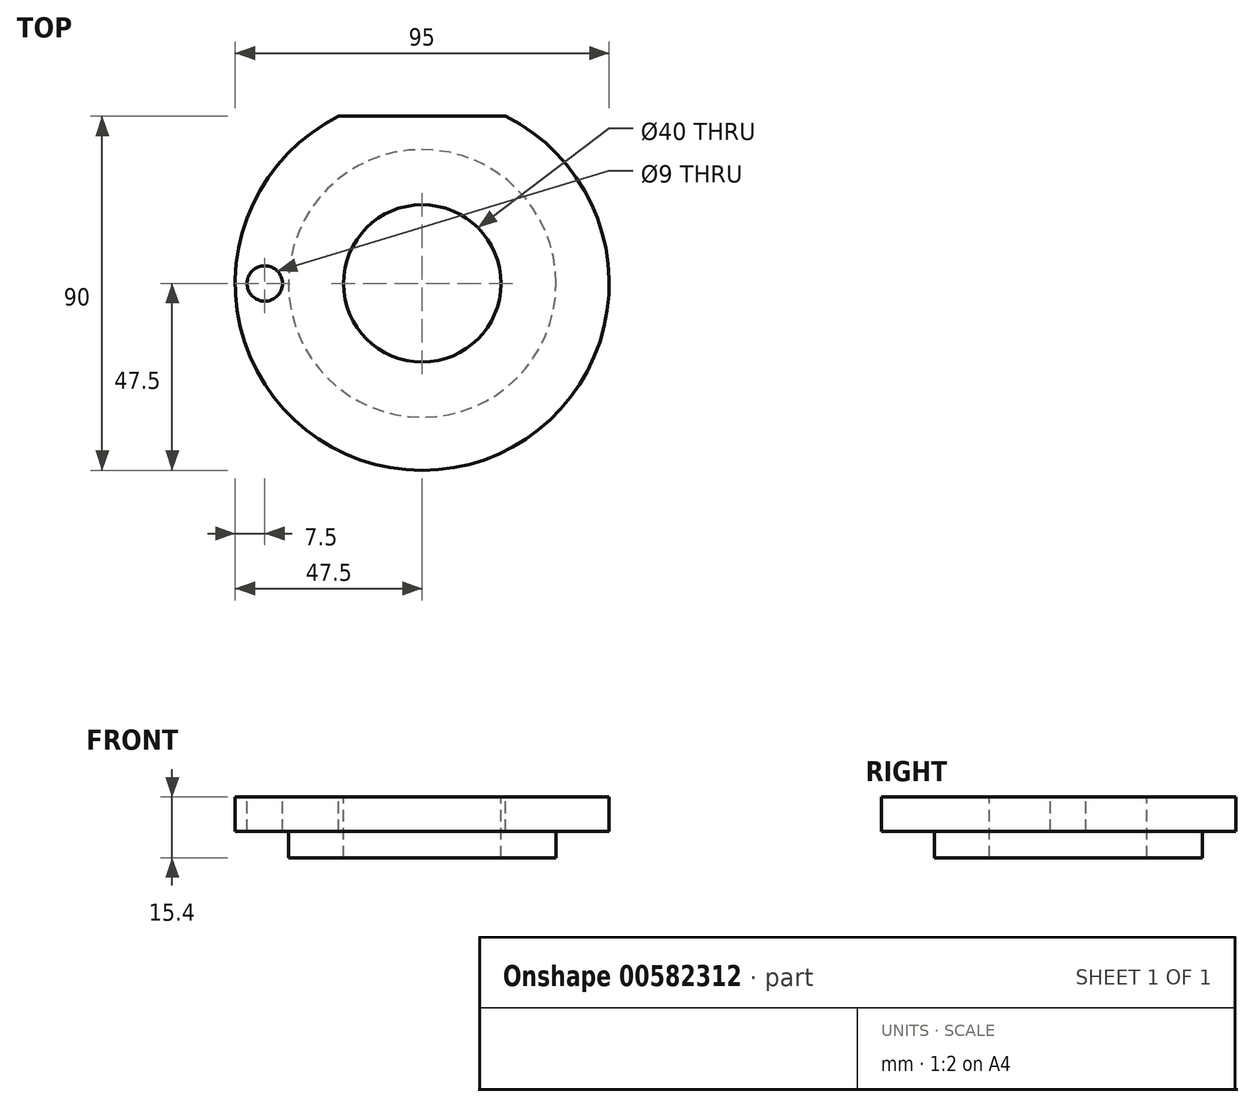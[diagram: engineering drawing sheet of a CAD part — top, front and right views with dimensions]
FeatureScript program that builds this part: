
annotation { "Feature Type Name" : "Feature", "Feature Type Description" : "" }
export const myFeature = defineFeature(function(context is Context, id is Id, definition is map)
    precondition{}
    {
        {
            var Q0;
            Q0=qCreatedBy(makeId("Top.planeOp"),FACE);
            var sketch = newSketch(context, id + "F0", { "sketchPlane" : qUnion([Q0])});
            skCircle(sketch, "E0", {"center": v(0, 0) * mm, "radius": 47.5 * mm});
            skSolve(sketch);
        }
        {
            var Q0;
            Q0=makeQuery(id+"F0.imprint","IMPRINT",FACE,{"disambiguationData":[TD([[makeQuery(id+"F0.imprint","IMPRINT",EDGE,{"derivedFrom":sQuery(id+"F0.wireOp",EDGE,"E0")}),1.0]])]});
            extrude(context, id + "F1", {"entities" : qUnion([Q0]), "oppositeDirection" : true, "depth" : 8.7 * mm, "offsetDistance" : 25 * mm});
        }
        {
            var Q0;
            Q0=makeQuery(id+"F1.opExtrude","CAP_FACE",FACE,{"disambiguationData":[OSD([sQuery(id+"F0.wireOp",EDGE,"E0")])],"isStart":true});
            var sketch = newSketch(context, id + "F2", { "sketchPlane" : qUnion([Q0])});
            skCircle(sketch, "E1", {"center": v(0, 0) * mm, "radius": 34 * mm});
            skSolve(sketch);
        }
        {
            var Q0;
            Q0 = qSketchRegion(id + "F2", true);
            extrude(context, id + "F3", {"entities" : qUnion([Q0]), "operationType" : NewBodyOperationType.ADD, "oppositeDirection" : true, "depth" : 15.4 * mm, "offsetDistance" : 25 * mm});
        }
        {
            var Q0;
            Q0=makeQuery(id+"F1.opExtrude","CAP_FACE",FACE,{"disambiguationData":[OSD([sQuery(id+"F0.wireOp",EDGE,"E0")])],"isStart":true});
            var sketch = newSketch(context, id + "F4", { "sketchPlane" : qUnion([Q0])});
            skCircle(sketch, "E2.0", {"center": v(0, 0) * mm, "radius": 47.5 * mm});
            skLineSegment(sketch, "E3", {"start": v(-21.21, 42.5) * mm, "end": v(21.21, 42.5) * mm});
            skSolve(sketch);
        }
        {
            var Q0;
            {var subQ0=sQuery(id+"F4.wireOp",EDGE,"E3");Q0=makeQuery(id+"F4.imprint","IMPRINT",FACE,{"disambiguationData":[TD([[makeQuery(id+"F4.imprint","IMPRINT",EDGE,{"derivedFrom":subQ0}),1.0]])]});}
            extrude(context, id + "F5", {"entities" : qUnion([Q0]), "operationType" : NewBodyOperationType.REMOVE, "endBound" : BoundingType.THROUGH_ALL, "oppositeDirection" : true, "depth" : 25 * mm, "offsetDistance" : 25 * mm});
        }
        {
            var Q0;
            Q0=makeQuery(id+"F1.opExtrude","CAP_FACE",FACE,{"disambiguationData":[OSD([sQuery(id+"F0.wireOp",EDGE,"E0")])],"isStart":true});
            var sketch = newSketch(context, id + "F6", { "sketchPlane" : qUnion([Q0])});
            skCircle(sketch, "E4", {"center": v(0, 0) * mm, "radius": 20 * mm});
            skSolve(sketch);
        }
        {
            var Q0;
            Q0=makeQuery(id+"F6.imprint","IMPRINT",FACE,{"disambiguationData":[TD([[makeQuery(id+"F6.imprint","IMPRINT",EDGE,{"derivedFrom":sQuery(id+"F6.wireOp",EDGE,"E4")}),1.0]])]});
            extrude(context, id + "F7", {"entities" : qUnion([Q0]), "operationType" : NewBodyOperationType.REMOVE, "endBound" : BoundingType.THROUGH_ALL, "oppositeDirection" : true, "depth" : 25 * mm, "offsetDistance" : 25 * mm});
        }
        {
            var Q0;
            Q0=makeQuery(id+"F1.opExtrude","CAP_FACE",FACE,{"disambiguationData":[OSD([sQuery(id+"F0.wireOp",EDGE,"E0")])],"isStart":true});
            var sketch = newSketch(context, id + "F8", { "sketchPlane" : qUnion([Q0])});
            skLineSegment(sketch, "E5", {"start": v(-40, 0) * mm, "end": v(40, 0) * mm, "construction": true});
            skPoint(sketch, "E6", {"position": v(-40, 0) * mm});
            skSolve(sketch);
        }
        {
            var Q0;
            Q0=sQuery(id+"F8.wireOp",VERTEX,"E6");
            var Q1;
            Q1=makeQuery(id+"F1.opExtrude","SWEPT_BODY",BODY,{"disambiguationData":[OSD([sQuery(id+"F0.wireOp",EDGE,"E0")])]});
            hole(context, id + "F9", {"style" : HoleStyle.SIMPLE, "endStyle" : HoleEndStyle.THROUGH, "holeDiameter" : 9 * mm, "majorDiameter" : 5 * mm, "isTappedThrough" : true, "tappedDepth" : 12 * mm, "tapClearance" : 3, "locations" : qUnion([Q0]), "scope" : qUnion([Q1])});
        }
        {
            var Q0;
            Q0=qCreatedBy(makeId("Front.planeOp"),FACE);
            var sketch = newSketch(context, id + "F10", { "sketchPlane" : qUnion([Q0])});
            skLineSegment(sketch, "E7", {"start": v(0, 0) * mm, "end": v(0, 49.3) * mm});
            skSolve(sketch);
        }
    });
